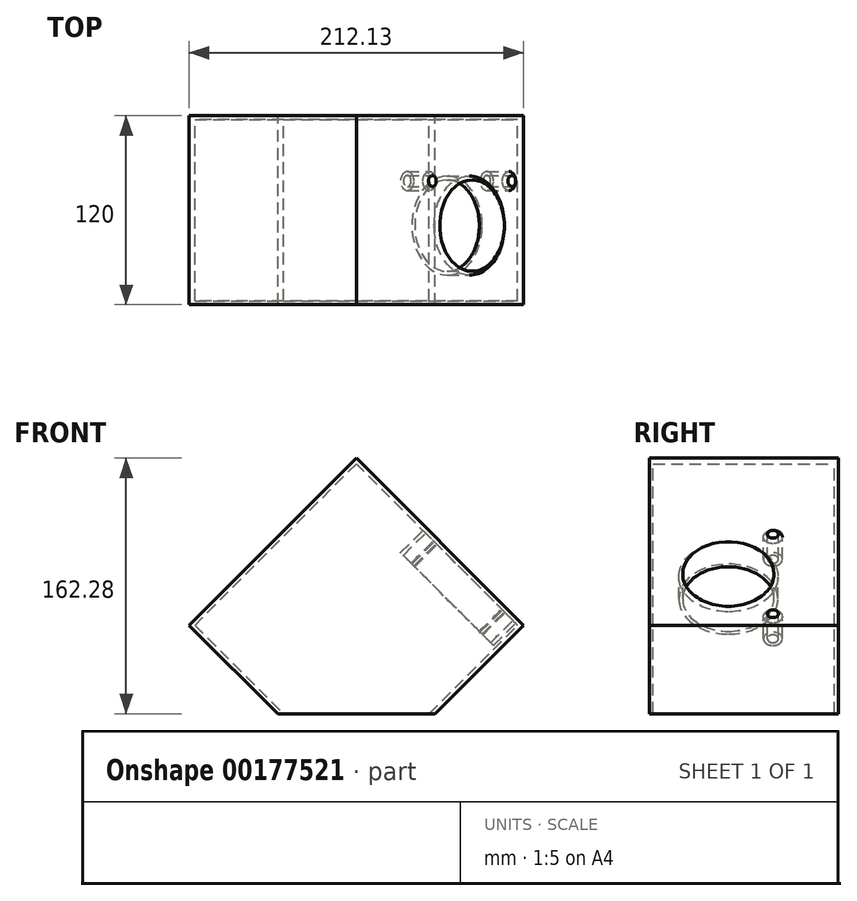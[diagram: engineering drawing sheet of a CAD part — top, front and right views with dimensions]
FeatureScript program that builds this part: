
annotation { "Feature Type Name" : "Feature", "Feature Type Description" : "" }
export const myFeature = defineFeature(function(context is Context, id is Id, definition is map)
    precondition{}
    {
        {
            var Q0;
            Q0=qCreatedBy(makeId("Front.planeOp"),FACE);
            var sketch = newSketch(context, id + "F0", { "sketchPlane" : qUnion([Q0])});
            skLineSegment(sketch, "E0", {"start": v(65.03, 0) * mm, "end": v(121.24, 56.22) * mm});
            skLineSegment(sketch, "E1", {"start": v(121.24, 56.22) * mm, "end": v(15.18, 162.28) * mm});
            skLineSegment(sketch, "E2", {"start": v(15.18, 162.28) * mm, "end": v(-90.89, 56.22) * mm});
            skLineSegment(sketch, "E3", {"start": v(-90.89, 56.22) * mm, "end": v(-34.67, 0) * mm});
            skLineSegment(sketch, "E4", {"start": v(-34.67, 0) * mm, "end": v(65.03, 0) * mm});
            skSolve(sketch);
        }
        {
            var Q0;
            Q0=makeQuery(id+"F0.imprint","IMPRINT",FACE,{"disambiguationData":[TD([[makeQuery(id+"F0.imprint","IMPRINT",EDGE,{"derivedFrom":sQuery(id+"F0.wireOp",EDGE,"E0")}),1.0]])]});
            extrude(context, id + "F1", {"entities" : qUnion([Q0]), "depth" : 120 * mm, "symmetric" : true});
        }
        {
            var Q0;
            Q0=makeQuery(id+"F1.opExtrude","SWEPT_FACE",FACE,{"disambiguationData":[OSD([sQuery(id+"F0.wireOp",EDGE,"E1")])]});
            var sketch = newSketch(context, id + "F2", { "sketchPlane" : qUnion([Q0])});
            skLineSegment(sketch, "E5.bottom", {"start": v(24.06, 43.2) * mm, "end": v(-80.44, 43.2) * mm});
            skLineSegment(sketch, "E5.top", {"start": v(24.06, -43.2) * mm, "end": v(-80.44, -43.2) * mm});
            skLineSegment(sketch, "E5.left", {"start": v(26.06, 41.2) * mm, "end": v(26.06, -41.2) * mm});
            skLineSegment(sketch, "E5.right", {"start": v(-82.44, 41.2) * mm, "end": v(-82.44, -41.2) * mm});
            skPoint(sketch, "E5.middle", {"position": v(-28.19, 0) * mm});
            skPoint(sketch, "E6.visualSharp", {"position": v(-82.44, -43.2) * mm});
            skArc(sketch, "E6.filletArc", {"start": v(-82.44, -41.2) * mm, "mid": v(-81.85, -42.61) * mm, "end": v(-80.44, -43.2) * mm});
            skPoint(sketch, "E7.visualSharp", {"position": v(-82.44, 43.2) * mm});
            skArc(sketch, "E7.filletArc", {"start": v(-80.44, 43.2) * mm, "mid": v(-81.85, 42.61) * mm, "end": v(-82.44, 41.2) * mm});
            skPoint(sketch, "E8.visualSharp", {"position": v(26.06, 43.2) * mm});
            skArc(sketch, "E8.filletArc", {"start": v(26.06, 41.2) * mm, "mid": v(25.48, 42.61) * mm, "end": v(24.06, 43.2) * mm});
            skPoint(sketch, "E9.visualSharp", {"position": v(26.06, -43.2) * mm});
            skArc(sketch, "E9.filletArc", {"start": v(24.06, -43.2) * mm, "mid": v(25.48, -42.61) * mm, "end": v(26.06, -41.2) * mm});
            skCircle(sketch, "E10", {"center": v(-9.74, 0) * mm, "radius": 29 * mm});
            skCircle(sketch, "E11", {"center": v(-74.94, -35.7) * mm, "radius": 3.5 * mm});
            skCircle(sketch, "E12", {"center": v(-74.94, 35.7) * mm, "radius": 3.5 * mm});
            skCircle(sketch, "E13", {"center": v(18.56, 35.7) * mm, "radius": 3.5 * mm});
            skCircle(sketch, "E14", {"center": v(18.56, -35.7) * mm, "radius": 3.5 * mm});
            skSolve(sketch);
        }
        {
            var Q0;
            Q0=makeQuery(id+"F2.imprint","IMPRINT",FACE,{"disambiguationData":[TD([[makeQuery(id+"F2.imprint","IMPRINT",EDGE,{"derivedFrom":sQuery(id+"F2.wireOp",EDGE,"E5.bottom")}),1.0]])]});
            var Q1;
            Q1=makeQuery(id+"F2.imprint","IMPRINT",FACE,{"disambiguationData":[TD([[makeQuery(id+"F2.imprint","IMPRINT",EDGE,{"derivedFrom":sQuery(id+"F2.wireOp",EDGE,"E10")}),1.0]])]});
            var Q2;
            Q2=makeQuery(id+"F2.imprint","IMPRINT",FACE,{"disambiguationData":[TD([[makeQuery(id+"F2.imprint","IMPRINT",EDGE,{"derivedFrom":sQuery(id+"F2.wireOp",EDGE,"E11")}),1.0]])]});
            var Q3;
            Q3=makeQuery(id+"F2.imprint","IMPRINT",FACE,{"disambiguationData":[TD([[makeQuery(id+"F2.imprint","IMPRINT",EDGE,{"derivedFrom":sQuery(id+"F2.wireOp",EDGE,"E12")}),1.0]])]});
            var Q4;
            Q4=makeQuery(id+"F2.imprint","IMPRINT",FACE,{"disambiguationData":[TD([[makeQuery(id+"F2.imprint","IMPRINT",EDGE,{"derivedFrom":sQuery(id+"F2.wireOp",EDGE,"E13")}),1.0]])]});
            var Q5;
            Q5=makeQuery(id+"F2.imprint","IMPRINT",FACE,{"disambiguationData":[TD([[makeQuery(id+"F2.imprint","IMPRINT",EDGE,{"derivedFrom":sQuery(id+"F2.wireOp",EDGE,"E14")}),1.0]])]});
            extrude(context, id + "F3", {"entities" : qUnion([Q0, Q1, Q2, Q3, Q4, Q5]), "operationType" : NewBodyOperationType.REMOVE, "oppositeDirection" : true, "depth" : 20 * mm});
        }
        {
            var Q0;
            Q0=makeQuery(id+"F1.opExtrude","SWEPT_FACE",FACE,{"disambiguationData":[OSD([sQuery(id+"F0.wireOp",EDGE,"E4")])]});
            shell(context, id + "F4", {"entities" : qUnion([Q0]), "thickness" : 2.5 * mm});
        }
        {
            var Q0;
            Q0=makeQuery(id+"F2.imprint","IMPRINT",FACE,{"disambiguationData":[TD([[makeQuery(id+"F2.imprint","IMPRINT",EDGE,{"derivedFrom":sQuery(id+"F2.wireOp",EDGE,"E10")}),1.0]])]});
            var Q1;
            Q1=makeQuery(id+"F2.imprint","IMPRINT",FACE,{"disambiguationData":[TD([[makeQuery(id+"F2.imprint","IMPRINT",EDGE,{"derivedFrom":sQuery(id+"F2.wireOp",EDGE,"E12")}),1.0]])]});
            var Q2;
            Q2=makeQuery(id+"F2.imprint","IMPRINT",FACE,{"disambiguationData":[TD([[makeQuery(id+"F2.imprint","IMPRINT",EDGE,{"derivedFrom":sQuery(id+"F2.wireOp",EDGE,"E11")}),1.0]])]});
            var Q3;
            Q3=makeQuery(id+"F2.imprint","IMPRINT",FACE,{"disambiguationData":[TD([[makeQuery(id+"F2.imprint","IMPRINT",EDGE,{"derivedFrom":sQuery(id+"F2.wireOp",EDGE,"E14")}),1.0]])]});
            var Q4;
            Q4=makeQuery(id+"F2.imprint","IMPRINT",FACE,{"disambiguationData":[TD([[makeQuery(id+"F2.imprint","IMPRINT",EDGE,{"derivedFrom":sQuery(id+"F2.wireOp",EDGE,"E13")}),1.0]])]});
            extrude(context, id + "F5", {"entities" : qUnion([Q0, Q1, Q2, Q3, Q4]), "operationType" : NewBodyOperationType.REMOVE, "oppositeDirection" : true, "depth" : 40 * mm});
        }
    });
